# Revit family: 206_Pelti-lapivienti
name_source: partatom
category: Duct Accessories
units: mm (PartAtom-declared; Revit-internal decimal feet)

## family parameters
Always vertical = Yes
Cut with Voids When Loaded = No
Part Type = Breaks Into
Round Connector Dimension = Use Diameter
Shared = No
Work Plane-Based = No

## types (1)
- VILPE STEEL PASS-THROUGH
    CAT0 = Yes
    D = 110 mm
    Description = Pass-through seal
    ET = 2 mm  [stored 0.00656168 ft]
    H2D = 280 mm
    L12 = 95 mm  [stored 0.31168 ft]
    L1W = 120 mm  [stored 0.393701 ft]
    L22 = 105 mm  [stored 0.344488 ft]
    L2D = 10 mm  [stored 0.0328084 ft]
    L2W = 130 mm  [stored 0.426509 ft]
    L32 = 115 mm  [stored 0.377297 ft]
    L3W = 140 mm  [stored 0.459318 ft]
    L45 = 260 mm  [stored 0.853018 ft]
    L452 = 125 mm  [stored 0.410105 ft]
    LLL = 5 mm  [stored 0.0164042 ft]
    MC Product Code = VILPE STEEL PASS-THROUGH
    Manufacturer = Vilpe
    QmdConnectorList = 201;D;202;D
    THW = 10 mm  [stored 0.0328084 ft]
    URL = http://www.vilpe.com
    W1 = 200 mm  [stored 0.656168 ft]
    W12 = 100 mm  [stored 0.328084 ft]
    W2 = 220 mm  [stored 0.721785 ft]
    W22 = 110 mm  [stored 0.360892 ft]
    W2D = 360 mm  [stored 1.1811 ft]
    W3 = 240 mm  [stored 0.787402 ft]
    W32 = 120 mm  [stored 0.393701 ft]
    W322 = 100 mm  [stored 0.328084 ft]
    W4 = 360 mm  [stored 1.1811 ft]
    W41 = 260 mm  [stored 0.853018 ft]
    WL = 90 mm  [stored 0.295276 ft]
    magiPartTypeId = 206
    magiProductFamilyId = Pelti-lapivienti
    magiProductId = Pelti-lapivienti

note: [stored X ft] marks values corroborated as IEEE doubles in the binary element streams (Revit-internal decimal feet)

## geometry (parser evidence)
native form markers: Sweep x2
no freeform markers — native parametric forms only
